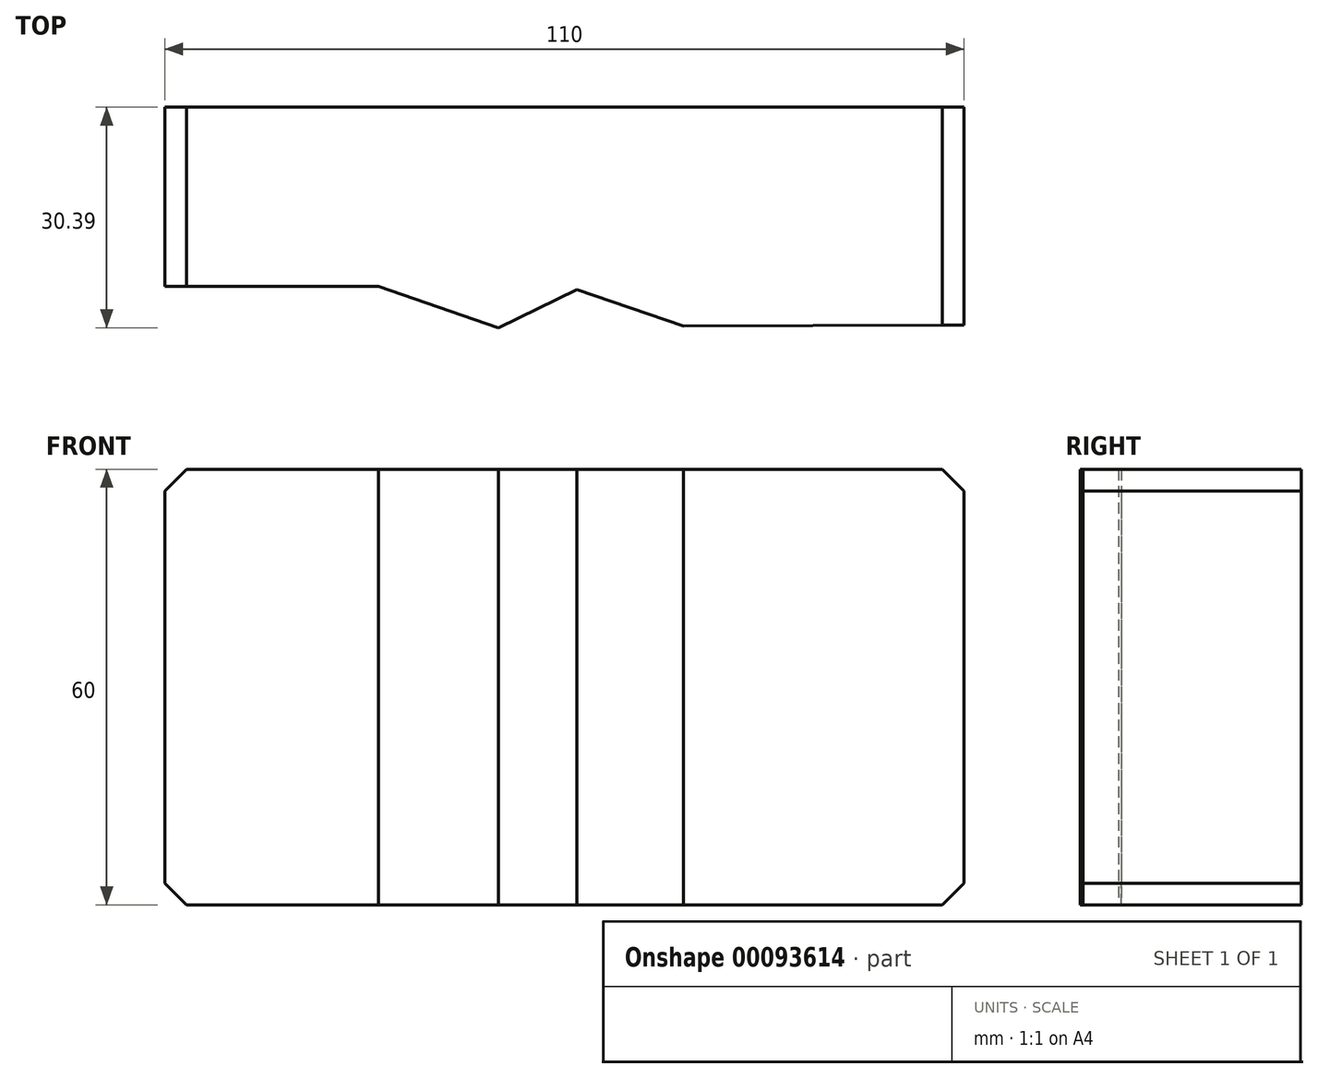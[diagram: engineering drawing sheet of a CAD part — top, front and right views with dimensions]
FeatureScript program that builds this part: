
annotation { "Feature Type Name" : "Feature", "Feature Type Description" : "" }
export const myFeature = defineFeature(function(context is Context, id is Id, definition is map)
    precondition{}
    {
        {
            var Q0;
            Q0=qCreatedBy(makeId("Top.planeOp"),FACE);
            var sketch = newSketch(context, id + "F0", { "sketchPlane" : qUnion([Q0])});
            skLineSegment(sketch, "E0", {"start": v(-52.8, 5.76) * mm, "end": v(57.2, 5.76) * mm});
            skLineSegment(sketch, "E1", {"start": v(-52.8, 5.76) * mm, "end": v(-52.8, -18.96) * mm});
            skLineSegment(sketch, "E2", {"start": v(57.2, 5.76) * mm, "end": v(57.2, -24.24) * mm});
            skLineSegment(sketch, "E3", {"start": v(-52.8, -18.96) * mm, "end": v(-23.4, -18.96) * mm});
            skLineSegment(sketch, "E4", {"start": v(-23.4, -18.96) * mm, "end": v(-6.9, -24.63) * mm});
            skLineSegment(sketch, "E5", {"start": v(-6.9, -24.63) * mm, "end": v(3.95, -19.34) * mm});
            skLineSegment(sketch, "E6", {"start": v(3.95, -19.34) * mm, "end": v(18.6, -24.38) * mm});
            skLineSegment(sketch, "E7", {"start": v(18.6, -24.38) * mm, "end": v(57.2, -24.24) * mm});
            skSolve(sketch);
        }
        {
            var Q0;
            Q0=makeQuery(id+"F0.imprint","IMPRINT",FACE,{"disambiguationData":[TD([[makeQuery(id+"F0.imprint","IMPRINT",EDGE,{"derivedFrom":sQuery(id+"F0.wireOp",EDGE,"E0")}),-1.0]])]});
            extrude(context, id + "F1", {"entities" : qUnion([Q0]), "depth" : 60 * mm});
        }
        {
            var Q0;
            Q0=makeQuery(id+"F1.opExtrude","CAP_EDGE",EDGE,{"disambiguationData":[OSD([sQuery(id+"F0.wireOp",EDGE,"E1")])],"isStart":false});
            var Q1;
            Q1=makeQuery(id+"F1.opExtrude","CAP_EDGE",EDGE,{"disambiguationData":[OSD([sQuery(id+"F0.wireOp",EDGE,"E1")])],"isStart":true});
            var Q2;
            Q2=makeQuery(id+"F1.opExtrude","CAP_EDGE",EDGE,{"disambiguationData":[OSD([sQuery(id+"F0.wireOp",EDGE,"E2")])],"isStart":false});
            var Q3;
            Q3=makeQuery(id+"F1.opExtrude","CAP_EDGE",EDGE,{"disambiguationData":[OSD([sQuery(id+"F0.wireOp",EDGE,"E2")])],"isStart":true});
            chamfer(context, id + "F2", {"entities" : qUnion([Q0, Q1, Q2, Q3]), "width" : 3 * mm, "tangentPropagation" : true});
        }
    });
